# Revit family: Trench_Frame-Watts-Dead_Level-DX-GF
name_source: partatom
category: Plumbing Fixtures
revit_build: Autodesk Revit 2014 (Build: 20130308_1515(x64)
units: mm (PartAtom-declared; Revit-internal decimal feet)

## types (1)
- Dead Level DX-GF
    - RGP Reinforced Galvanized Perforated = No
    - RGS Reinforced Galvanized Slotted = No
    - RSP Reinforced Stainless Steel Perforated = No
    - RSS Reinforced Stainless Steel Slotted = No
    - SCI Solid Cast Iron = No
    -DI Ductile Iron Grate = No
    -DI-ADA Ductile Iron ADA grate = No
    -GDI Galvanized Ductile Iron = No
    Anchor Lug Array = 4
    Anchor Lug Array Spacing = 11.667 "
    Assembly Code = D2030
    CW Connection = No
    CWFU = 0
    Country = United States
    Default Elevation = 0 "
    Description = Watts Dead Level DX-GF 12 in(305mm) wide x 48 in(1219mm) long (standard) ductile iron frame, with rust-resistant oil-black coating, and (specify) grating to suit DIN Class (specify) load rating. System to include frame connectors, grate lockdowns, and construction covers.
    Grate Array = 48
    Grate Array Dist. = 0.625 "
    Grate Array Spacing = 1.25 "
    Grate Material = Metal-WATTS-Ductile Iron
    HW Connection = No
    HWFU = 0
    Height = 3 "
    Length = 48 "
    Manufacturer = WATTS
    Manufacturer Product Line = Drainage Products
    Material = Metal-WATTS-Ductile Iron
    Model = Dead Level DX-GF
    Product Documentation Link = http://media.wattswater.com
    Product Page URL = http://www.watts.com
    Region = North America
    URL = http://www.watts.com
    Vent Connection = No
    WFU = 0
    Waste Connection = Yes
    Width = 11.75 "

## geometry (parser evidence)
native form markers: Sweep x5
no freeform markers — native parametric forms only
